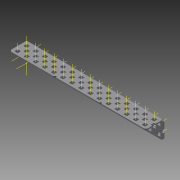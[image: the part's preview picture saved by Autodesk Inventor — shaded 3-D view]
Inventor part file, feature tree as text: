
AUTODESK INVENTOR PART (.ipt)
format: ipt  version: 2015 (Build 190159000, 159)  size: 2,084,352 bytes
history: native  units: in
note: dims shown in document units (in); Inventor stores cm internally (conversion verified against a paired STEP export)
features: other x95, pattern_linear x4, sheet_metal_op x1, extrude x1, imported_body x1, sketch x1
ambient origin geometry x8: Origin, YZ Plane, XZ Plane, XY Plane, X Axis, Y Axis, Z Axis, Center Point
bodies: Body1 (feature_tree)
feature tree (103):
  sheet_metal_op  "Fold1"
  other  "L-Channel"
  extrude  "length cut"  Depth=0.5in
  other  "top out axis"
  other  "top inner axis"
  other  "back out axis"
  other  "back inner axis"
  pattern_linear  "top outer axes"  Count1=2 Spacing1=0.5in
  pattern_linear  "top inner axes"  Spacing1=0.5in  [1 undecoded]
  pattern_linear  "back outer axes"  Count1=2 Spacing1=0.5in
  pattern_linear  "back inner axes"  Spacing1=0.5in  [1 undecoded]
  other  "right plane"
  imported_body  "Base1"
  sketch  "Sketch1"  dims[d1=0.0in d4=0.5in d5=0.7874in d7=0.5in d10=0.5in d13=0.5in d14=0.7874in d16=0.5in d19=0.5in d20=-7.5in d21=0.0in d22=0.0in d23=0.0in d24=0.0in d25=0.0in d26=0.0in]
  other  "Work Point1"
  other  "Work Point2"
  other  "Work Point3"
  other  "Work Point4"
  other  "Work Axis5"
  other  "Work Axis6"
  other  "Work Axis7"
  other  "Work Axis8"
  other  "Work Axis11"
  other  "Work Axis12"
  other  "Work Axis13"
  other  "Work Axis14"
  other  "Work Axis15"
  other  "Work Axis18"
  other  "Work Axis19"
  other  "Work Axis20"
  other  "Work Axis23"
  other  "Work Axis24"
  other  "Work Axis25"
  other  "Work Axis26"
  other  "Work Axis29"
  other  "Work Axis30"
  other  "Work Axis31"
  other  "Work Axis32"
  other  "Work Axis33"
  other  "Work Axis36"
  other  "Work Axis37"
  other  "Work Axis38"
  other  "Work Axis41"
  other  "Work Axis42"
  other  "Work Axis43"
  other  "Work Axis44"
  other  "Work Axis45"
  other  "Work Axis61"
  other  "Work Axis62"
  other  "Work Axis63"
  other  "Work Axis64"
  other  "Work Axis65"
  other  "Work Axis81"
  other  "Work Axis82"
  other  "Work Axis83"
  other  "Work Axis84"
  other  "Work Axis85"
  other  "Work Axis101"
  other  "Work Axis102"
  other  "Work Axis103"
  other  "Work Axis104"
  other  "Work Axis105"
  other  "Work Axis121"
  other  "Work Axis122"
  other  "Work Axis123"
  other  "Work Axis124"
  other  "Work Axis125"
  other  "Work Axis141"
  other  "Work Axis142"
  other  "Work Axis143"
  other  "Work Axis144"
  other  "Work Axis145"
  other  "left plane"
  other  "Work Axis161"
  other  "Work Axis162"
  other  "Work Axis163"
  other  "Work Axis164"
  other  "Work Axis165"
  other  "Work Axis166"
  other  "Work Axis167"
  other  "Work Axis168"
  other  "Work Axis169"
  other  "Work Axis170"
  other  "Work Axis171"
  other  "Work Axis172"
  other  "Work Axis173"
  other  "Work Axis174"
  other  "Work Axis175"
  other  "Work Axis176"
  other  "Work Axis177"
  other  "Work Axis178"
  other  "Work Axis179"
  other  "Work Axis180"
  other  "Work Axis181"
  other  "Work Axis182"
  other  "Work Axis183"
  other  "Work Axis184"
  other  "Work Axis185"
  other  "Work Axis186"
  other  "Work Axis187"
  other  "Work Axis188"
  other  "Work Axis189"
  other  "Work Axis190"
note: 2 required parameter values undecoded (feature->parameter linkage not recoverable at this tier; creation-order binding heuristic only, values carry confidence <= 0.55)
